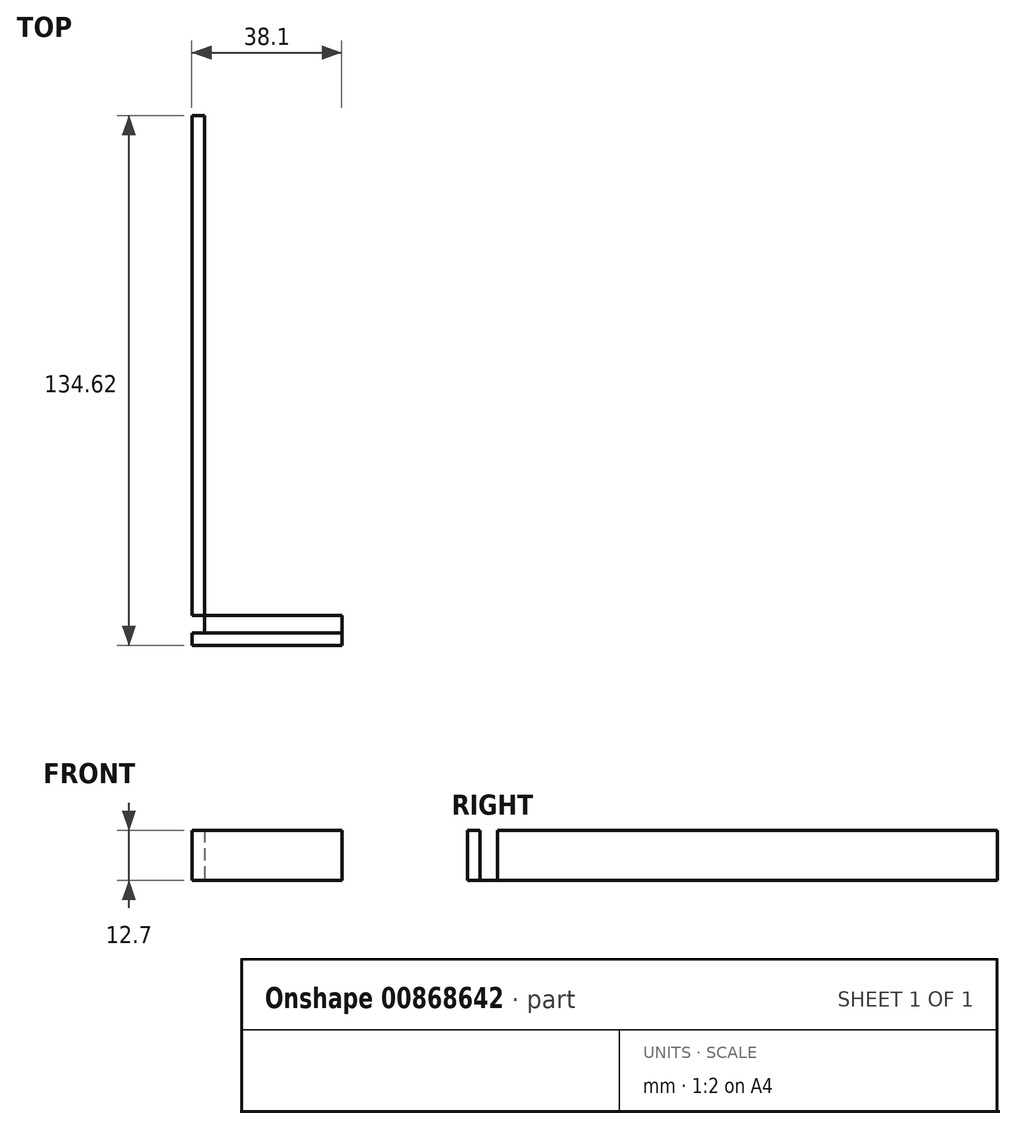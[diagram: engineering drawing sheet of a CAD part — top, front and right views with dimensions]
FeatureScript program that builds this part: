
annotation { "Feature Type Name" : "Feature", "Feature Type Description" : "" }
export const myFeature = defineFeature(function(context is Context, id is Id, definition is map)
    precondition{}
    {
        {
            var Q0;
            Q0=qCreatedBy(makeId("Top.planeOp"),FACE);
            var sketch = newSketch(context, id + "F0", { "sketchPlane" : qUnion([Q0])});
            skLineSegment(sketch, "E0.bottom", {"start": v(-3.18, 127) * mm, "end": v(0, 127) * mm});
            skLineSegment(sketch, "E0.top", {"start": v(-3.18, 0) * mm, "end": v(0, 0) * mm});
            skLineSegment(sketch, "E0.left", {"start": v(-3.18, 127) * mm, "end": v(-3.18, 0) * mm});
            skLineSegment(sketch, "E0.right", {"start": v(0, 127) * mm, "end": v(0, 0) * mm});
            skLineSegment(sketch, "E1.bottom", {"start": v(-3.18, 0) * mm, "end": v(34.93, 0) * mm});
            skLineSegment(sketch, "E1.top", {"start": v(-3.17, -7.62) * mm, "end": v(34.93, -7.62) * mm});
            skLineSegment(sketch, "E1.left", {"start": v(-3.18, 0) * mm, "end": v(-3.17, -7.62) * mm});
            skLineSegment(sketch, "E1.right", {"start": v(34.93, 0) * mm, "end": v(34.93, -7.62) * mm});
            skLineSegment(sketch, "E2.bottom", {"start": v(-3.17, -4.45) * mm, "end": v(34.93, -4.45) * mm});
            skLineSegment(sketch, "E2.left", {"start": v(-3.18, -4.45) * mm, "end": v(-3.17, -7.62) * mm});
            skLineSegment(sketch, "E2.right", {"start": v(34.93, -4.45) * mm, "end": v(34.93, -7.62) * mm});
            skLineSegment(sketch, "E3.bottom", {"start": v(0, 0) * mm, "end": v(-3.18, 0) * mm});
            skLineSegment(sketch, "E3.top", {"start": v(0, -7.62) * mm, "end": v(-3.17, -7.62) * mm});
            skLineSegment(sketch, "E3.left", {"start": v(0, 0) * mm, "end": v(0, -7.62) * mm});
            skSolve(sketch);
        }
        {
            var Q0;
            Q0=makeQuery(id+"F0.imprint","IMPRINT",FACE,{"disambiguationData":[TD([[makeQuery(id+"F0.imprint","IMPRINT",EDGE,{"derivedFrom":sQuery(id+"F0.wireOp",EDGE,"E0.bottom")}),-1.0]])]});
            var Q1;
            {var subQ5=sQuery(id+"F0.wireOp",EDGE,"E3.bottom");Q1=makeQuery(id+"F0.imprint","IMPRINT",FACE,{"disambiguationData":[TD([[makeQuery(id+"F0.imprint","IMPRINT",EDGE,{"derivedFrom":subQ5}),1.0]])]});}
            var Q2;
            {var subQ5=sQuery(id+"F0.wireOp",EDGE,"E3.top");Q2=makeQuery(id+"F0.imprint","IMPRINT",FACE,{"disambiguationData":[TD([[makeQuery(id+"F0.imprint","IMPRINT",EDGE,{"derivedFrom":subQ5}),-1.0]])]});}
            var Q3;
            {var subQ4=sQuery(id+"F0.wireOp",EDGE,"E1.top");Q3=makeQuery(id+"F0.imprint","IMPRINT",FACE,{"disambiguationData":[TD([[makeQuery(id+"F0.imprint","IMPRINT",EDGE,{"derivedFrom":subQ4}),1.0]])]});}
            extrude(context, id + "F1", {"entities" : qUnion([Q0, Q1, Q2, Q3]), "depth" : 12.7 * mm, "offsetDistance" : 25.4 * mm});
        }
        {
            var Q0;
            {var subQ0=sQuery(id+"F0.wireOp",EDGE,"E1.bottom");Q0=makeQuery(id+"F0.imprint","IMPRINT",FACE,{"disambiguationData":[TD([[makeQuery(id+"F0.imprint","IMPRINT",EDGE,{"derivedFrom":subQ0}),-1.0]])]});}
            extrude(context, id + "F2", {"entities" : qUnion([Q0]), "operationType" : NewBodyOperationType.ADD, "depth" : 1 / 203.2 * mm, "offsetDistance" : 25.4 * mm});
        }
    });
